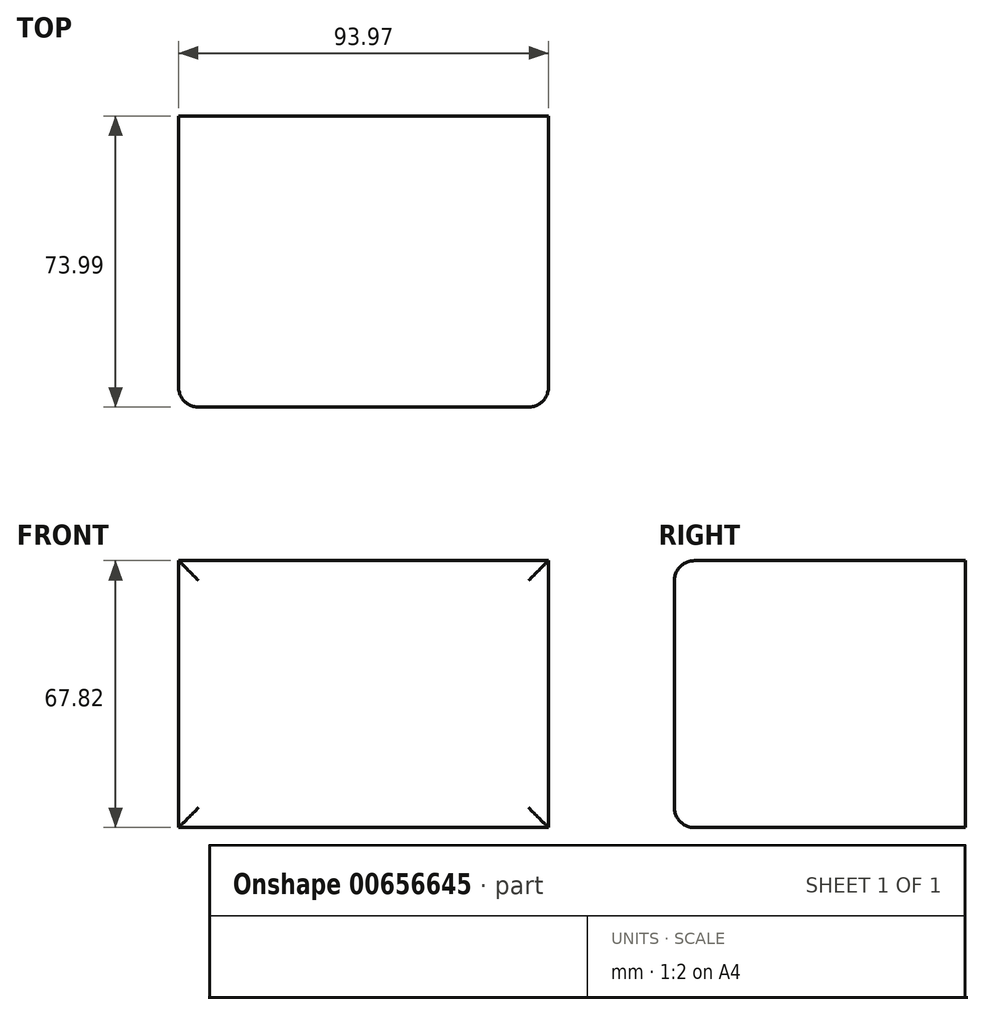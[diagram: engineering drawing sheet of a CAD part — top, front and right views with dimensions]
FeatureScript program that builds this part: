
annotation { "Feature Type Name" : "Feature", "Feature Type Description" : "" }
export const myFeature = defineFeature(function(context is Context, id is Id, definition is map)
    precondition{}
    {
        {
            var Q0;
            Q0=qCreatedBy(makeId("Front.planeOp"),FACE);
            var sketch = newSketch(context, id + "F0", { "sketchPlane" : qUnion([Q0])});
            skLineSegment(sketch, "E0.bottom", {"start": v(-99.47, 176.52) * mm, "end": v(0, 176.52) * mm});
            skLineSegment(sketch, "E0.top", {"start": v(-99.47, 131.91) * mm, "end": v(0, 131.91) * mm});
            skLineSegment(sketch, "E0.left", {"start": v(-99.47, 176.52) * mm, "end": v(-99.47, 131.91) * mm});
            skLineSegment(sketch, "E0.right", {"start": v(0, 176.52) * mm, "end": v(0, 131.91) * mm});
            skLineSegment(sketch, "E1.bottom", {"start": v(93.97, -145.38) * mm, "end": v(0, -145.38) * mm});
            skLineSegment(sketch, "E1.top", {"start": v(93.97, -213.2) * mm, "end": v(0, -213.2) * mm});
            skLineSegment(sketch, "E1.left", {"start": v(93.97, -145.38) * mm, "end": v(93.97, -213.2) * mm});
            skLineSegment(sketch, "E1.right", {"start": v(0, -145.38) * mm, "end": v(0, -213.2) * mm});
            skLineSegment(sketch, "E2.bottom", {"start": v(22.3, 89.8) * mm, "end": v(0, 89.8) * mm});
            skLineSegment(sketch, "E2.top", {"start": v(22.3, 176.52) * mm, "end": v(0, 176.52) * mm});
            skLineSegment(sketch, "E2.left", {"start": v(22.3, 89.8) * mm, "end": v(22.3, 176.52) * mm});
            skLineSegment(sketch, "E2.right", {"start": v(0, 89.8) * mm, "end": v(0, 176.52) * mm});
            skSolve(sketch);
        }
        {
            var Q0;
            Q0=makeQuery(id+"F0.imprint","IMPRINT",FACE,{"disambiguationData":[TD([[makeQuery(id+"F0.imprint","IMPRINT",EDGE,{"derivedFrom":sQuery(id+"F0.wireOp",EDGE,"E1.bottom")}),1.0]])]});
            extrude(context, id + "F1", {"entities" : qUnion([Q0]), "depth" : 74 * mm, "offsetDistance" : 25.4 * mm});
        }
        {
            var Q0;
            Q0=makeQuery(id+"F1.opExtrude","CAP_FACE",FACE,{"disambiguationData":[OSD([sQuery(id+"F0.wireOp",EDGE,"E1.bottom"),sQuery(id+"F0.wireOp",EDGE,"E1.top"),sQuery(id+"F0.wireOp",EDGE,"E1.left"),sQuery(id+"F0.wireOp",EDGE,"E1.right")])],"isStart":false});
            fillet(context, id + "F2", {"entities" : qUnion([Q0]), "radius" : 5.08 * mm, "tangentPropagation" : true, "allowEdgeOverflow" : false});
        }
    });
